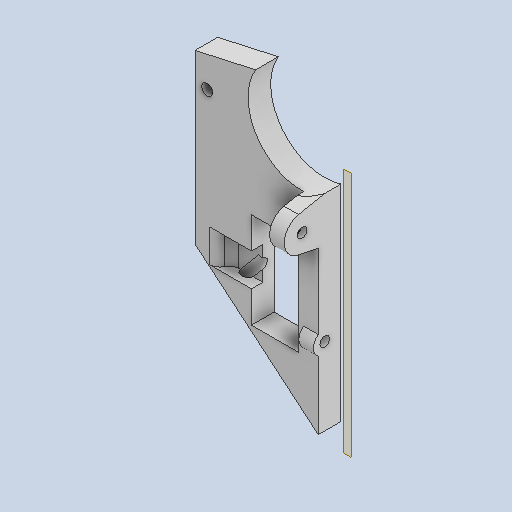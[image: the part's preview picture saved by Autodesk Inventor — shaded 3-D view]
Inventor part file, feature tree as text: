
AUTODESK INVENTOR PART (.ipt)
format: ipt  version: 2023 (Build 270158000, 158)  size: 296,448 bytes
history: native  units: in
note: dims shown in document units (in); Inventor stores cm internally (conversion verified against a paired STEP export)
features: reference x18, sketch x17, other x10, extrude x5, hole x2, projected_geometry x2, fillet x1
ambient origin geometry x8: Origin, YZ Plane, XZ Plane, XY Plane, X Axis, Y Axis, Z Axis, Center Point
bodies: Body1 (feature_tree)
feature tree (55):
  other  "SCIANA_2.0.ipt"
  extrude  "Wyciągnięcie proste1"  Depth=0.3937in
  extrude  "Wyciągnięcie proste2"  Depth=0.2362in
  extrude  "Wyciągnięcie proste3"  Depth=0.3937in TaperAngle=0.0deg
  fillet  "Zaokrąglenie1"  Radius=0.1378in
  hole  "Otwór1"  [1 undecoded]
  extrude  "Wyciągnięcie proste4"  Depth=0.1378in TaperAngle=0.0deg
  hole  "Otwór2"  [1 undecoded]
  extrude  "Wyciągnięcie proste5"  Depth=0.1181in
  other  "Bryła1::SCIANA_2.0.ipt"
  other  "Bryła wyprowadzona1"
  sketch  "Szkic1"
  sketch  "Szkic2"
  sketch  "Szkic3"
  sketch  "Szkic4"
  sketch  "Szkic5"
  sketch  "Szkic6"
  sketch  "Szkic7"
  sketch  "Szkic8"
  sketch  "Szkic9"
  sketch  "Szkic10"
  other  "Płaszczyzna konstrukcyjna1"
  other  "Płaszczyzna konstrukcyjna2"
  sketch  "Szkic11"
  reference  "Odniesienie1"
  reference  "Odniesienie2"
  reference  "Odniesienie3"
  reference  "Odniesienie4"
  reference  "Odniesienie5"
  reference  "Odniesienie6"
  reference  "Odniesienie7"
  reference  "Odniesienie8"
  reference  "Odniesienie9"
  sketch  "Szkic12"
  reference  "Odniesienie10"
  sketch  "Szkic13"
  reference  "Odniesienie11"
  reference  "Odniesienie12"
  sketch  "Szkic14"
  reference  "Odniesienie13"
  reference  "Odniesienie14"
  reference  "Odniesienie15"
  sketch  "Szkic15"
  reference  "Odniesienie16"
  reference  "Odniesienie17"
  reference  "Odniesienie18"
  sketch  "Szkic16"
  projected_geometry  "Pętla rzutowana1"
  sketch  "Szkic17"
  projected_geometry  "Pętla rzutowana2"
  other  "Bryła1"
  other  "GP2Y0A41SK0F_MIR1:1"
  other  "SCIANA_2.0:1"
  other  "mocowanie_serw:1"
  other  "pokrywka:1"
note: 2 required parameter values undecoded (feature->parameter linkage not recoverable at this tier; creation-order binding heuristic only, values carry confidence <= 0.55)
